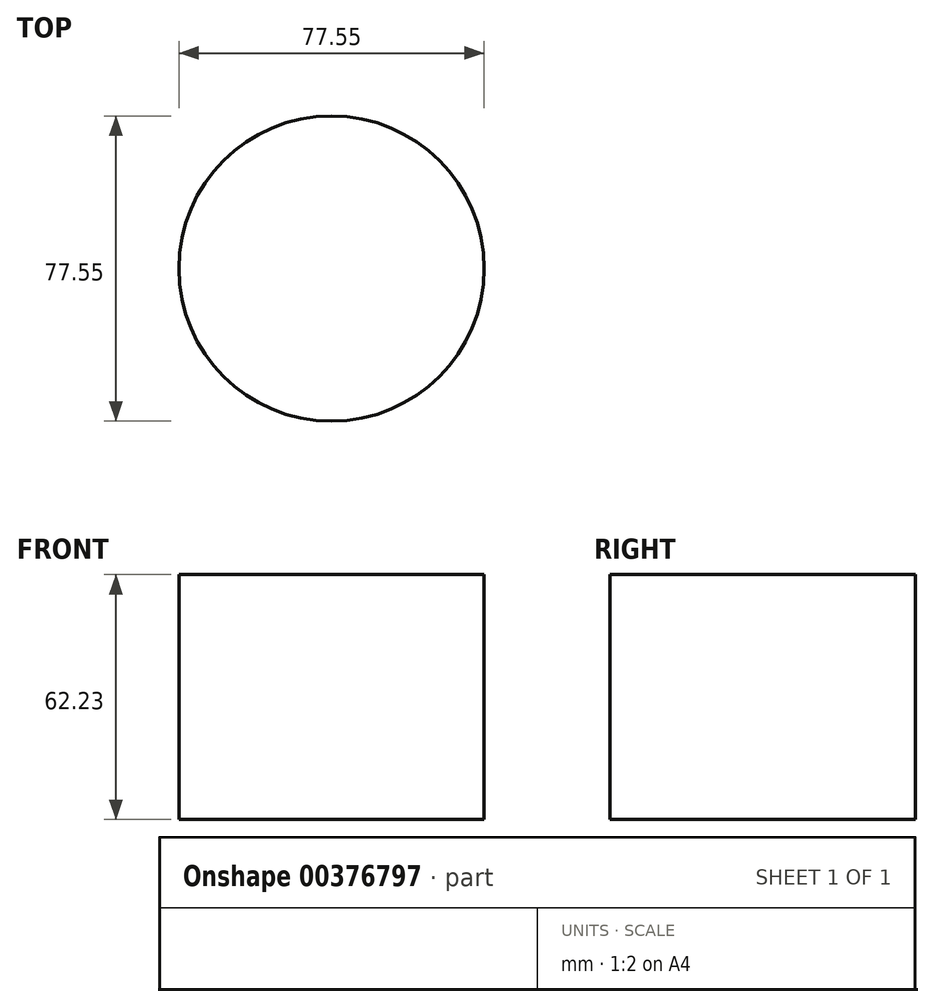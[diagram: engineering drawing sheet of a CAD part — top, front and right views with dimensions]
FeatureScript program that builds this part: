
annotation { "Feature Type Name" : "Feature", "Feature Type Description" : "" }
export const myFeature = defineFeature(function(context is Context, id is Id, definition is map)
    precondition{}
    {
        {
            var Q0;
            Q0=qCreatedBy(makeId("Top.planeOp"),FACE);
            var sketch = newSketch(context, id + "F0", { "sketchPlane" : qUnion([Q0])});
            skCircle(sketch, "E0", {"center": v(-61.82, -49.02) * mm, "radius": 38.78 * mm});
            skSolve(sketch);
        }
        {
            var Q0;
            Q0 = qSketchRegion(id + "F0", true);
            extrude(context, id + "F1", {"entities" : qUnion([Q0]), "depth" : 62.23 * mm});
        }
    });
